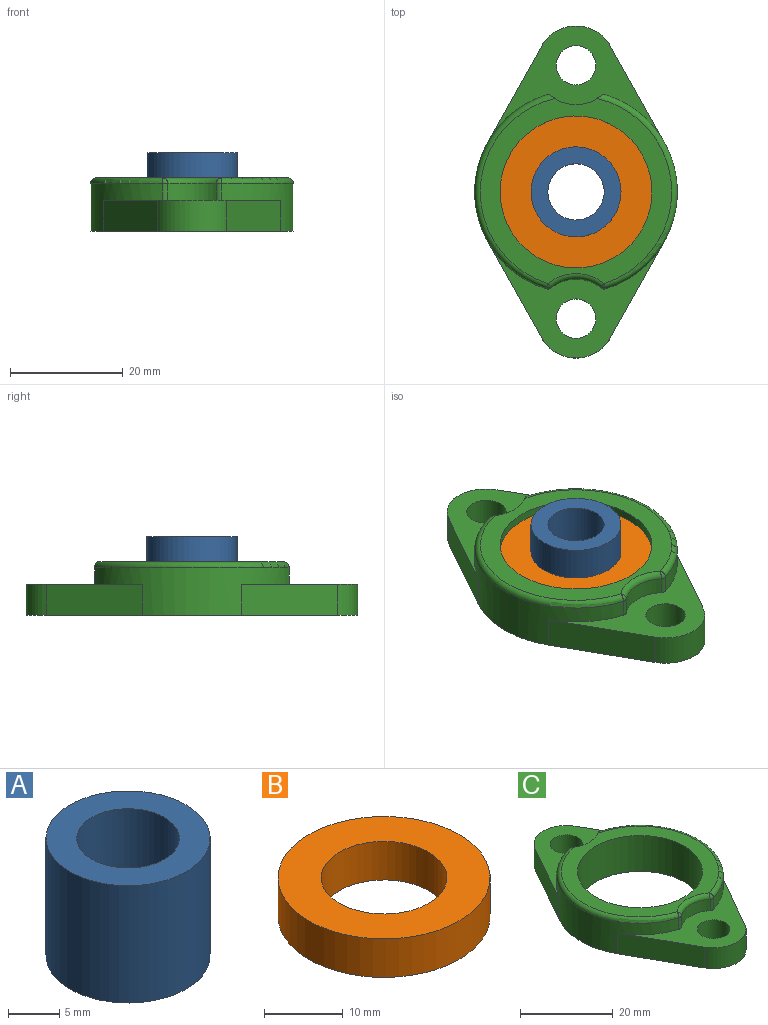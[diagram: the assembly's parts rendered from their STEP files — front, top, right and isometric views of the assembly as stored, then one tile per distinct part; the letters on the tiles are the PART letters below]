
ASSEMBLY  parts=3 mates=2
PART A: 4 faces, bbox 16x16x14 mm
  f0: cylinder r=5mm len=14mm, axis (0,0,-1), area 439.8mm2, adj f2,f3
  f1: cylinder r=8mm len=16mm, axis (0,0,-1), area 703.7mm2, adj f2,f3
  f2: plane 16x16mm, normal (0,0,1), area 122.5mm2, adj f0,f1
  f3: plane 16x16mm, normal (0,0,-1), area 122.5mm2, adj f0,f1
PART B: 4 faces, bbox 27x27x6 mm
  f0: cylinder r=13.5mm len=27mm, axis (0,0,-1), area 508.9mm2, adj f2,f3
  f1: cylinder r=8mm len=16mm, axis (0,0,-1), area 301.6mm2, adj f2,f3
  f2: plane 27x27mm, normal (0,0,1), area 371.5mm2, adj f0,f1
  f3: plane 27x27mm, normal (0,0,-1), area 371.5mm2, adj f0,f1
PART C: 26 faces, bbox 39x59x9.5 mm
  f0: plane 31.4x20.7mm, normal (0,0,1), area 177mm2, adj f1,f2,f3,f4,f5,f11,f14,f17
  f1: cylinder r=18mm len=34.41mm, axis (0,0,-1), area 238.6mm2, adj f0,f2,f10,f12,f13,f21,f24,f25
  f2: plane 17.12x9.6mm, normal (0.87,0.49,0), area 108mm2, adj f0,f1,f3,f13
  f3: cylinder r=7mm len=12.21mm, axis (0,0,-1), area 81.6mm2, adj f0,f2,f4,f13
  f4: plane 17.12x9.6mm, normal (-0.87,0.49,0), area 108mm2, adj f0,f3,f5,f13
  f5: cylinder r=18mm len=34.41mm, axis (0,0,-1), area 238.6mm2, adj f0,f4,f6,f12,f13,f17,f18,f19
  f6: plane 17.12x9.6mm, normal (-0.87,-0.49,0), area 108mm2, adj f5,f7,f12,f13
  f7: cylinder r=7mm len=12.21mm, axis (0,0,-1), area 81.6mm2, adj f6,f10,f12,f13
  f8: cylinder r=3.5mm len=7mm, axis (0,0,-1), area 121mm2, adj f12,f13
  f9: cylinder r=13.5mm len=27mm, axis (0,0,-1), area 805.8mm2, adj f13,f16
  f10: plane 17.12x9.6mm, normal (0.87,-0.49,0), area 108mm2, adj f1,f7,f12,f13
  f11: cylinder r=3.5mm len=7mm, axis (0,0,-1), area 121mm2, adj f0,f13
  f12: plane 31.4x20.7mm, normal (0,0,1), area 177mm2, adj f1,f5,f6,f7,f8,f10,f15,f18
  f13: plane 59x36mm, normal (0,0,-1), area 766.8mm2, adj f1,f2,f3,f4,f5,f6,f7,f8
  f14: cylinder r=7mm len=8.74mm, axis (0,0,-1), area 37.7mm2, adj f0,f16,f17,f19,f24,f25
  f15: cylinder r=7mm len=8.74mm, axis (0,0,-1), area 28.3mm2, adj f12,f18,f21,f22
  f16: plane 34x32.83mm, normal (0,0,1), area 310.8mm2, adj f9,f14,f19,f22,f24
  f17: cylinder r=1mm len=3.81mm, axis (0,0,1), area 3.3mm2, adj f0,f5,f14,f19
  f18: cylinder r=1mm len=3mm, axis (0,0,1), area 2.9mm2, adj f5,f12,f15,f20
  f19: torus R=17mm, axis (0,0,1), area 71.6mm2, adj f5,f14,f16,f17,f20
  f20: sphere r=1mm, area 1mm2, adj f18,f19,f22
  f21: cylinder r=1mm len=3mm, axis (0,0,1), area 2.9mm2, adj f1,f12,f15,f23
  f22: torus R=8mm, axis (0,0,1), area 15.6mm2, adj f15,f16,f20,f23
  f23: sphere r=1mm, area 1mm2, adj f21,f22,f24
  f24: torus R=17mm, axis (0,0,1), area 71.6mm2, adj f1,f14,f16,f23,f25
  f25: cylinder r=1mm len=3.81mm, axis (0,0,1), area 3.3mm2, adj f0,f1,f14,f24
PLACE A t=(0,0,-4.49)mm fixed
PLACE B t=(0,0,-3.99)mm
PLACE C t=(0,0,-4.49)mm
MATE fastened C.f9 <-> A.f0  axis (0,0,-1) through (0,0,-4.49)mm
MATE fastened B.f1 <-> A.f0  axis (0,0,-1) through (0,0,-4.49)mm
